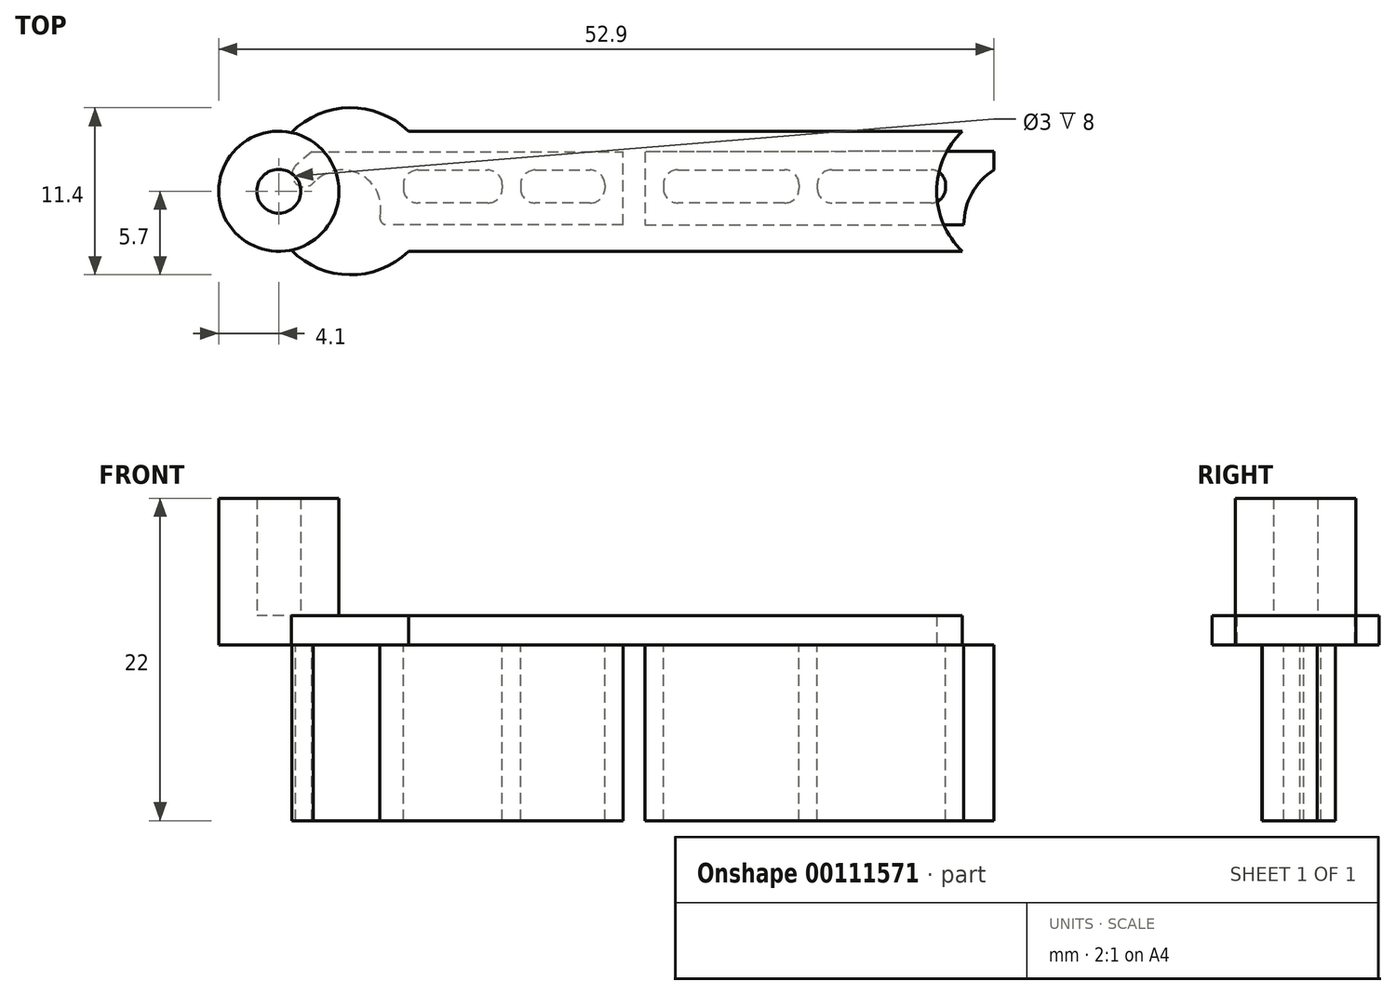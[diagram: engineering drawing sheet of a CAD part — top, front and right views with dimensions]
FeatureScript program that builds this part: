
annotation { "Feature Type Name" : "Feature", "Feature Type Description" : "" }
export const myFeature = defineFeature(function(context is Context, id is Id, definition is map)
    precondition{}
    {
        {
            var Q0;
            Q0=qCreatedBy(makeId("Top.planeOp"),FACE);
            var sketch = newSketch(context, id + "F0", { "sketchPlane" : qUnion([Q0])});
            skLineSegment(sketch, "E0.bottom", {"start": v(-24.06, 4.1) * mm, "end": v(21.64, 4.1) * mm});
            skLineSegment(sketch, "E0.top", {"start": v(-24.06, -4.1) * mm, "end": v(21.64, -4.1) * mm});
            skArc(sketch, "E1", {"start": v(-24.15, 4.01) * mm, "mid": v(-29.1, 0) * mm, "end": v(-24.15, -4.01) * mm});
            skArc(sketch, "E2", {"start": v(-24.15, -4.01) * mm, "mid": v(-20.16, -5.7) * mm, "end": v(-16.14, -4.1) * mm});
            skArc(sketch, "E3", {"start": v(21.64, 4.1) * mm, "mid": v(19.9, 0) * mm, "end": v(21.64, -4.1) * mm});
            skArc(sketch, "E4.trimOffspring", {"start": v(-16.14, 4.1) * mm, "mid": v(-20.16, 5.7) * mm, "end": v(-24.15, 4.01) * mm});
            skSolve(sketch);
        }
        {
            var Q0;
            Q0 = qSketchRegion(id + "F0", true);
            extrude(context, id + "F1", {"entities" : qUnion([Q0]), "depth" : 2 * mm});
        }
        {
            var Q0;
            Q0=makeQuery(id+"F1.opExtrude","CAP_FACE",FACE,{"disambiguationData":[OSD([sQuery(id+"F0.wireOp",EDGE,"E0.bottom"),sQuery(id+"F0.wireOp",EDGE,"E0.top"),sQuery(id+"F0.wireOp",EDGE,"E1"),sQuery(id+"F0.wireOp",EDGE,"E2"),sQuery(id+"F0.wireOp",EDGE,"E3"),sQuery(id+"F0.wireOp",EDGE,"E4.trimOffspring")])],"isStart":false});
            var sketch = newSketch(context, id + "F2", { "sketchPlane" : qUnion([Q0])});
            skCircle(sketch, "E5", {"center": v(-25, 0) * mm, "radius": 4.1 * mm});
            skCircle(sketch, "E6", {"center": v(-25, 0) * mm, "radius": 1.5 * mm});
            skSolve(sketch);
        }
        {
            var Q0;
            Q0 = qSketchRegion(id + "F2", true);
            extrude(context, id + "F3", {"entities" : qUnion([Q0]), "operationType" : NewBodyOperationType.ADD, "depth" : 8 * mm});
        }
        {
            var Q0;
            Q0=makeQuery(id+"F1.opExtrude","CAP_FACE",FACE,{"disambiguationData":[OSD([sQuery(id+"F0.wireOp",EDGE,"E0.bottom"),sQuery(id+"F0.wireOp",EDGE,"E0.top"),sQuery(id+"F0.wireOp",EDGE,"E1"),sQuery(id+"F0.wireOp",EDGE,"E2"),sQuery(id+"F0.wireOp",EDGE,"E3"),sQuery(id+"F0.wireOp",EDGE,"E4.trimOffspring")])],"isStart":true});
            var sketch = newSketch(context, id + "F4", { "sketchPlane" : qUnion([Q0])});
            skLineSegment(sketch, "E7", {"start": v(-22.76, -2.7) * mm, "end": v(-23.86, -1.74) * mm});
            skPoint(sketch, "E8.center.orphan", {"position": v(-23.25, -1.15) * mm});
            skArc(sketch, "E9", {"start": v(-23.86, -1.74) * mm, "mid": v(-23.84, -0.54) * mm, "end": v(-22.64, -0.56) * mm});
            skLineSegment(sketch, "E10.right", {"start": v(-2.75, -0.45) * mm, "end": v(-2.75, -0.2) * mm});
            skLineSegment(sketch, "E11.left", {"start": v(-16.5, -0.45) * mm, "end": v(-16.5, -0.2) * mm});
            skLineSegment(sketch, "E12.trimOffspring", {"start": v(-15.5, -1.45) * mm, "end": v(-10.75, -1.45) * mm});
            skLineSegment(sketch, "E13.left", {"start": v(-8.5, -0.45) * mm, "end": v(-8.5, -0.2) * mm});
            skLineSegment(sketch, "E13.right", {"start": v(-9.75, -0.45) * mm, "end": v(-9.75, -0.2) * mm});
            skLineSegment(sketch, "E14.trimOffspring", {"start": v(-7.5, -1.45) * mm, "end": v(-3.75, -1.45) * mm});
            skLineSegment(sketch, "E15.left", {"start": v(0, -2.7) * mm, "end": v(0, 2.3) * mm});
            skLineSegment(sketch, "E15.right", {"start": v(1.25, -0.47) * mm, "end": v(1.25, -0.2) * mm});
            skLineSegment(sketch, "E16", {"start": v(2.25, -1.47) * mm, "end": v(9.5, -1.47) * mm});
            skLineSegment(sketch, "E17.left", {"start": v(11.75, -0.47) * mm, "end": v(11.75, -0.2) * mm});
            skLineSegment(sketch, "E18.trimOffspring", {"start": v(12.75, -1.47) * mm, "end": v(19.5, -1.47) * mm});
            skArc(sketch, "E19", {"start": v(-22.52, -0.68) * mm, "mid": v(-19.42, -1.14) * mm, "end": v(-18.09, 1.7) * mm});
            skPoint(sketch, "E20.visualSharp", {"position": v(-16.5, -1.45) * mm});
            skArc(sketch, "E20.filletArc", {"start": v(-16.5, -0.45) * mm, "mid": v(-16.2, -1.16) * mm, "end": v(-15.5, -1.45) * mm});
            skLineSegment(sketch, "E21.top", {"start": v(-10.75, 0.8) * mm, "end": v(-15.5, 0.8) * mm});
            skPoint(sketch, "E22.visualSharp", {"position": v(-16.5, 0.8) * mm});
            skArc(sketch, "E22.filletArc", {"start": v(-15.5, 0.8) * mm, "mid": v(-16.2, 0.5) * mm, "end": v(-16.5, -0.2) * mm});
            skArc(sketch, "E23.filletArc", {"start": v(-9.75, -0.2) * mm, "mid": v(-10.04, 0.5) * mm, "end": v(-10.75, 0.8) * mm});
            skPoint(sketch, "E24.visualSharp", {"position": v(-9.75, -1.45) * mm});
            skArc(sketch, "E24.filletArc", {"start": v(-10.75, -1.45) * mm, "mid": v(-10.04, -1.16) * mm, "end": v(-9.75, -0.45) * mm});
            skPoint(sketch, "E25.visualSharp", {"position": v(-8.5, -1.45) * mm});
            skArc(sketch, "E25.filletArc", {"start": v(-8.5, -0.45) * mm, "mid": v(-8.2, -1.16) * mm, "end": v(-7.5, -1.45) * mm});
            skLineSegment(sketch, "E26", {"start": v(-3.75, 0.8) * mm, "end": v(-7.5, 0.8) * mm});
            skPoint(sketch, "E27.visualSharp", {"position": v(-8.5, 0.8) * mm});
            skArc(sketch, "E27.filletArc", {"start": v(-7.5, 0.8) * mm, "mid": v(-8.2, 0.5) * mm, "end": v(-8.5, -0.2) * mm});
            skPoint(sketch, "E28.visualSharp", {"position": v(-2.75, 0.8) * mm});
            skArc(sketch, "E28.filletArc", {"start": v(-2.75, -0.2) * mm, "mid": v(-3.04, 0.5) * mm, "end": v(-3.75, 0.8) * mm});
            skPoint(sketch, "E29.visualSharp", {"position": v(-2.75, -1.45) * mm});
            skArc(sketch, "E29.filletArc", {"start": v(-3.75, -1.45) * mm, "mid": v(-3.04, -1.16) * mm, "end": v(-2.75, -0.45) * mm});
            skPoint(sketch, "E30.visualSharp", {"position": v(-18.29, 2.3) * mm});
            skArc(sketch, "E30.filletArc", {"start": v(-17.6, 2.3) * mm, "mid": v(-17.99, 2.12) * mm, "end": v(-18.09, 1.7) * mm});
            skPoint(sketch, "E31.visualSharp", {"position": v(1.25, -1.47) * mm});
            skArc(sketch, "E31.filletArc", {"start": v(1.25, -0.47) * mm, "mid": v(1.54, -1.18) * mm, "end": v(2.25, -1.47) * mm});
            skArc(sketch, "E32", {"start": v(21.75, 2.28) * mm, "mid": v(22.3, 0.14) * mm, "end": v(23.8, -1.47) * mm});
            skLineSegment(sketch, "E33.top", {"start": v(19.5, 0.8) * mm, "end": v(12.75, 0.8) * mm});
            skLineSegment(sketch, "E34.trimOffspring", {"start": v(1.25, 2.28) * mm, "end": v(1.25, 2.3) * mm});
            skLineSegment(sketch, "E35.trimOffspring", {"start": v(11.75, 2.28) * mm, "end": v(11.75, 2.3) * mm});
            skLineSegment(sketch, "E36", {"start": v(10.5, -0.47) * mm, "end": v(10.5, -0.2) * mm});
            skLineSegment(sketch, "E37.trimOffspring", {"start": v(10.5, 2.28) * mm, "end": v(10.5, 2.3) * mm});
            skLineSegment(sketch, "E38.trimOffspring", {"start": v(9.5, 0.8) * mm, "end": v(2.25, 0.8) * mm});
            skPoint(sketch, "E39.right.end.orphan", {"position": v(20.5, 0) * mm});
            skLineSegment(sketch, "E40", {"start": v(20.5, -0.47) * mm, "end": v(20.5, -0.2) * mm});
            skPoint(sketch, "E41.visualSharp", {"position": v(1.25, 0.8) * mm});
            skArc(sketch, "E41.filletArc", {"start": v(2.25, 0.8) * mm, "mid": v(1.54, 0.5) * mm, "end": v(1.25, -0.2) * mm});
            skPoint(sketch, "E42.visualSharp", {"position": v(10.5, 0.8) * mm});
            skArc(sketch, "E42.filletArc", {"start": v(10.5, -0.2) * mm, "mid": v(10.2, 0.5) * mm, "end": v(9.5, 0.8) * mm});
            skPoint(sketch, "E43.visualSharp", {"position": v(10.5, -1.47) * mm});
            skArc(sketch, "E43.filletArc", {"start": v(9.5, -1.47) * mm, "mid": v(10.2, -1.18) * mm, "end": v(10.5, -0.47) * mm});
            skPoint(sketch, "E44.visualSharp", {"position": v(11.75, -1.47) * mm});
            skArc(sketch, "E44.filletArc", {"start": v(11.75, -0.47) * mm, "mid": v(12.04, -1.18) * mm, "end": v(12.75, -1.47) * mm});
            skPoint(sketch, "E45.visualSharp", {"position": v(11.75, 0.8) * mm});
            skArc(sketch, "E45.filletArc", {"start": v(12.75, 0.8) * mm, "mid": v(12.04, 0.5) * mm, "end": v(11.75, -0.2) * mm});
            skPoint(sketch, "E46.visualSharp", {"position": v(20.5, 0.8) * mm});
            skArc(sketch, "E46.filletArc", {"start": v(20.5, -0.2) * mm, "mid": v(20.2, 0.5) * mm, "end": v(19.5, 0.8) * mm});
            skPoint(sketch, "E47.visualSharp", {"position": v(20.5, -1.47) * mm});
            skArc(sketch, "E47.filletArc", {"start": v(19.5, -1.47) * mm, "mid": v(20.2, -1.18) * mm, "end": v(20.5, -0.47) * mm});
            skLineSegment(sketch, "E48", {"start": v(-1.5, 2.3) * mm, "end": v(-17.6, 2.3) * mm});
            skLineSegment(sketch, "E49", {"start": v(0, 2.3) * mm, "end": v(21.75, 2.28) * mm});
            skLineSegment(sketch, "E50", {"start": v(23.8, -1.47) * mm, "end": v(23.8, -2.72) * mm});
            skLineSegment(sketch, "E51", {"start": v(23.8, -2.72) * mm, "end": v(0, -2.7) * mm});
            skLineSegment(sketch, "E52", {"start": v(-1.5, 2.3) * mm, "end": v(-1.5, -2.7) * mm});
            skLineSegment(sketch, "E53", {"start": v(-22.76, -2.7) * mm, "end": v(-1.5, -2.7) * mm});
            skLineSegment(sketch, "E54", {"start": v(-22.64, -0.56) * mm, "end": v(-22.52, -0.68) * mm});
            skSolve(sketch);
        }
        {
            var Q0;
            Q0 = qSketchRegion(id + "F4", true);
            extrude(context, id + "F5", {"entities" : qUnion([Q0]), "operationType" : NewBodyOperationType.ADD, "depth" : 12 * mm});
        }
    });
